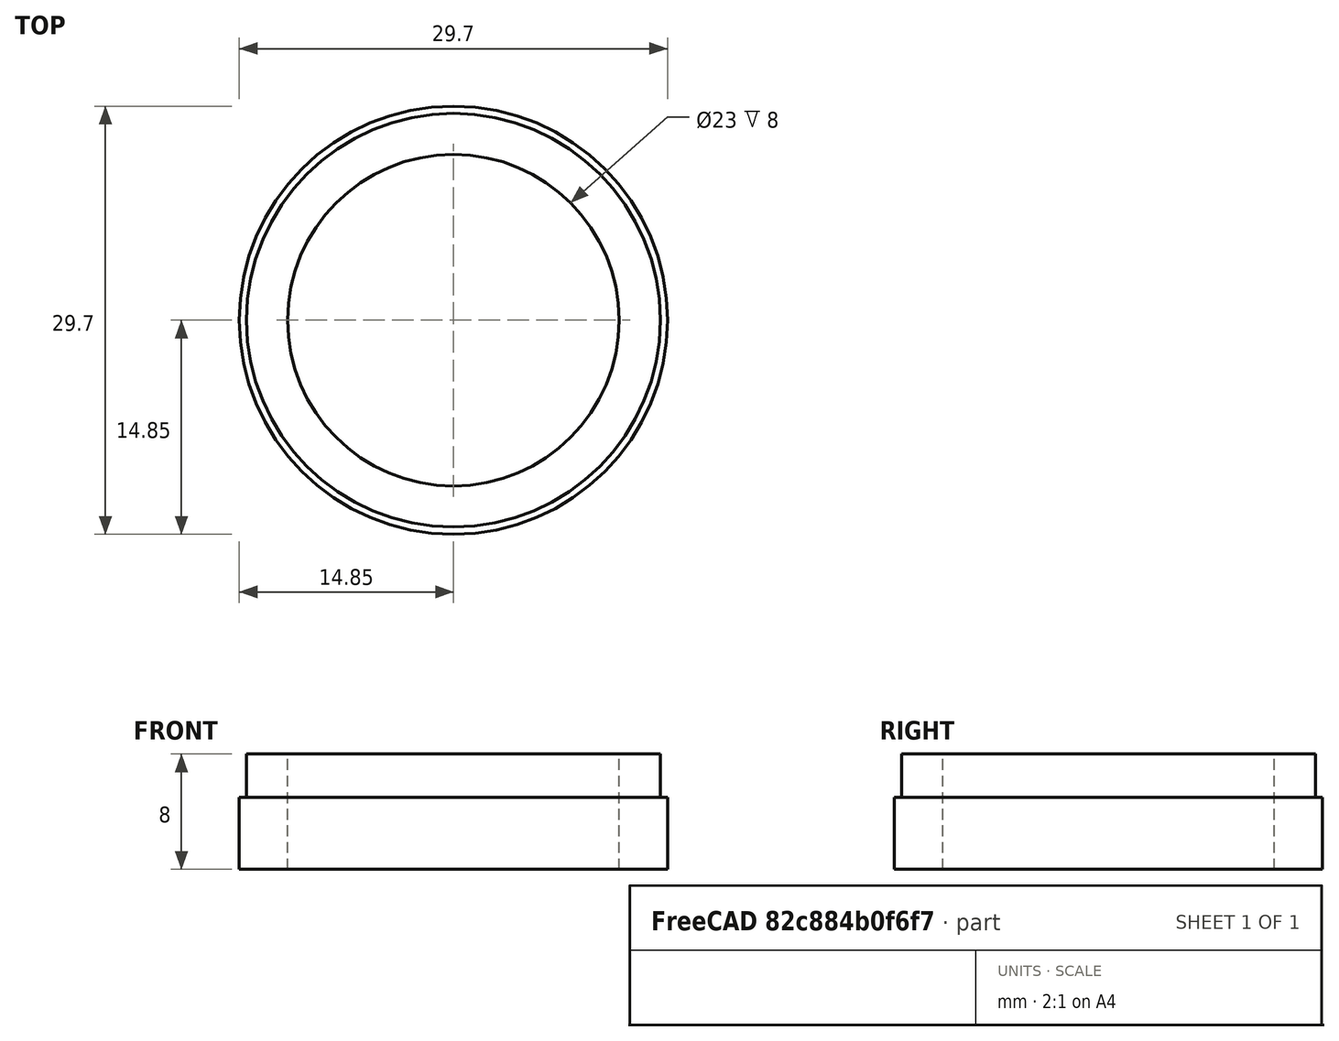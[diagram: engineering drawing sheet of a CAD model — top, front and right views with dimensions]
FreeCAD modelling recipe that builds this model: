
FCSTD DOCUMENT  (FreeCAD 0.16R6712 (Git))
Label: innerconnector
License: All rights reserved
LicenseURL: http://en.wikipedia.org/wiki/All_rights_reserved
objects: Part::Cylinder×3, Part::FeaturePython×2
note: 5 computed .brp shape members not serialized (recipe doc carries the construction recipe); baked Part::Feature solids carry a one-line shape summary decoded from their .brp

FEATURE [Part::Cylinder] Cylinder  label="圆柱体"
  Angle = 360
  Height = 5
  Radius = 14.85
FEATURE [Part::Cylinder] Cylinder001  label="圆柱体001"
  Angle = 360
  Height = 3
  Placement = pos=(0,0,5) rot=(0,0,1;0rad)
  Radius = 14.35
FEATURE [Part::Cylinder] Cylinder002  label="圆柱体002"
  Angle = 360
  Height = 10
  Radius = 11.5
FEATURE [Part::FeaturePython] Connect  # WARN: FeaturePython — macro-defined, semantics opaque (R4)
  Base = -> Cylinder
  Mode = 1
  Tool = -> Cylinder001
FEATURE [Part::FeaturePython] Cutout  # WARN: FeaturePython — macro-defined, semantics opaque (R4)
  Base = -> Connect
  Mode = 3
  Tool = -> Cylinder002
